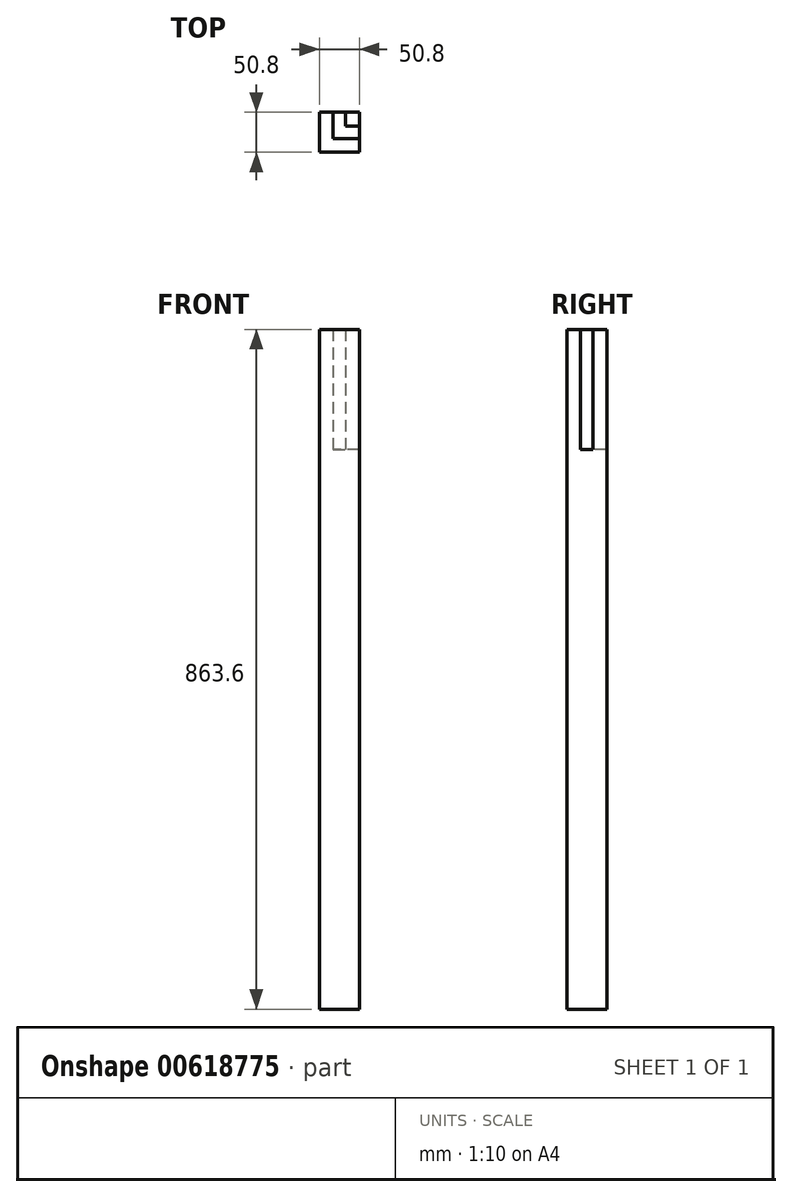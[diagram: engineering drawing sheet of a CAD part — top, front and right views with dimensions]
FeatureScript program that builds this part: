
annotation { "Feature Type Name" : "Feature", "Feature Type Description" : "" }
export const myFeature = defineFeature(function(context is Context, id is Id, definition is map)
    precondition{}
    {
        {
            var Q0;
            Q0=qCreatedBy(makeId("Top.planeOp"),FACE);
            var sketch = newSketch(context, id + "F0", { "sketchPlane" : qUnion([Q0])});
            skLineSegment(sketch, "E0.bottom", {"start": v(-28.48, -19.62) * mm, "end": v(22.32, -19.62) * mm});
            skLineSegment(sketch, "E0.top", {"start": v(-28.48, 31.18) * mm, "end": v(-11.02, 31.18) * mm});
            skLineSegment(sketch, "E0.left", {"start": v(-28.48, -19.62) * mm, "end": v(-28.48, 31.18) * mm});
            skLineSegment(sketch, "E0.right", {"start": v(22.32, -19.62) * mm, "end": v(22.32, -2.16) * mm});
            skLineSegment(sketch, "E1", {"start": v(22.32, 13.72) * mm, "end": v(4.85, 13.72) * mm});
            skLineSegment(sketch, "E2", {"start": v(22.32, -2.16) * mm, "end": v(-3.08, -2.16) * mm});
            skLineSegment(sketch, "E3", {"start": v(-11.02, 31.18) * mm, "end": v(-11.02, -2.16) * mm});
            skLineSegment(sketch, "E4", {"start": v(4.85, 31.18) * mm, "end": v(4.85, 13.72) * mm});
            skLineSegment(sketch, "E5", {"start": v(-3.08, -2.16) * mm, "end": v(-11.02, -2.16) * mm});
            skPoint(sketch, "E6.orphan", {"position": v(-3.08, -19.62) * mm});
            skLineSegment(sketch, "E7.trimOffspring", {"start": v(22.32, 13.72) * mm, "end": v(22.32, 31.18) * mm});
            skLineSegment(sketch, "E8.trimOffspring", {"start": v(-3.08, 31.18) * mm, "end": v(22.32, 31.18) * mm});
            skSolve(sketch);
        }
        {
            var Q0;
            Q0=makeQuery(id+"F0.imprint","IMPRINT",FACE,{"disambiguationData":[TD([[makeQuery(id+"F0.imprint","IMPRINT",EDGE,{"derivedFrom":sQuery(id+"F0.wireOp",EDGE,"E0.bottom")}),1.0]])]});
            var Q1;
            Q1=makeQuery(id+"F0.imprint","IMPRINT",FACE,{"disambiguationData":[TD([[makeQuery(id+"F0.imprint","IMPRINT",EDGE,{"derivedFrom":sQuery(id+"F0.wireOp",EDGE,"E1")}),-1.0]])]});
            extrude(context, id + "F1", {"entities" : qUnion([Q0, Q1]), "depth" : 152.4 * mm, "offsetDistance" : 25.4 * mm});
        }
        {
            var Q0;
            Q0=makeQuery(id+"F1.opExtrude","CAP_FACE",FACE,{"disambiguationData":[OSD([sQuery(id+"F0.wireOp",EDGE,"E0.bottom"),sQuery(id+"F0.wireOp",EDGE,"E0.top"),sQuery(id+"F0.wireOp",EDGE,"E0.left"),sQuery(id+"F0.wireOp",EDGE,"E0.right"),sQuery(id+"F0.wireOp",EDGE,"E2"),sQuery(id+"F0.wireOp",EDGE,"E3"),sQuery(id+"F0.wireOp",EDGE,"E5")])],"isStart":true});
            var sketch = newSketch(context, id + "F2", { "sketchPlane" : qUnion([Q0])});
            skLineSegment(sketch, "E9.bottom", {"start": v(-28.48, 19.62) * mm, "end": v(22.32, 19.62) * mm});
            skLineSegment(sketch, "E9.top", {"start": v(-28.48, -31.18) * mm, "end": v(22.32, -31.18) * mm});
            skLineSegment(sketch, "E9.left", {"start": v(-28.48, 19.62) * mm, "end": v(-28.48, -31.18) * mm});
            skLineSegment(sketch, "E9.right", {"start": v(22.32, 19.62) * mm, "end": v(22.32, -31.18) * mm});
            skSolve(sketch);
        }
        {
            var Q0;
            {var subQ1=makeQuery(id+"F1.opExtrude","CAP_EDGE",EDGE,{"disambiguationData":[OSD([sQuery(id+"F0.wireOp",EDGE,"E3")])],"isStart":true});Q0=makeQuery(id+"F2.imprint","IMPRINT",FACE,{"disambiguationData":[TD([[makeQuery(id+"F2.imprint","IMPRINT",EDGE,{"derivedFrom":subQ1}),-1.0]])]});}
            var Q1;
            {var subQ1=sQuery(id+"F2.wireOp",EDGE,"E9.bottom");Q1=makeQuery(id+"F2.imprint","IMPRINT",FACE,{"disambiguationData":[TD([[makeQuery(id+"F2.imprint","IMPRINT",EDGE,{"derivedFrom":subQ1}),-1.0]])]});}
            extrude(context, id + "F3", {"entities" : qUnion([Q0, Q1]), "operationType" : NewBodyOperationType.ADD, "depth" : 711.2 * mm, "offsetDistance" : 25.4 * mm});
        }
    });
